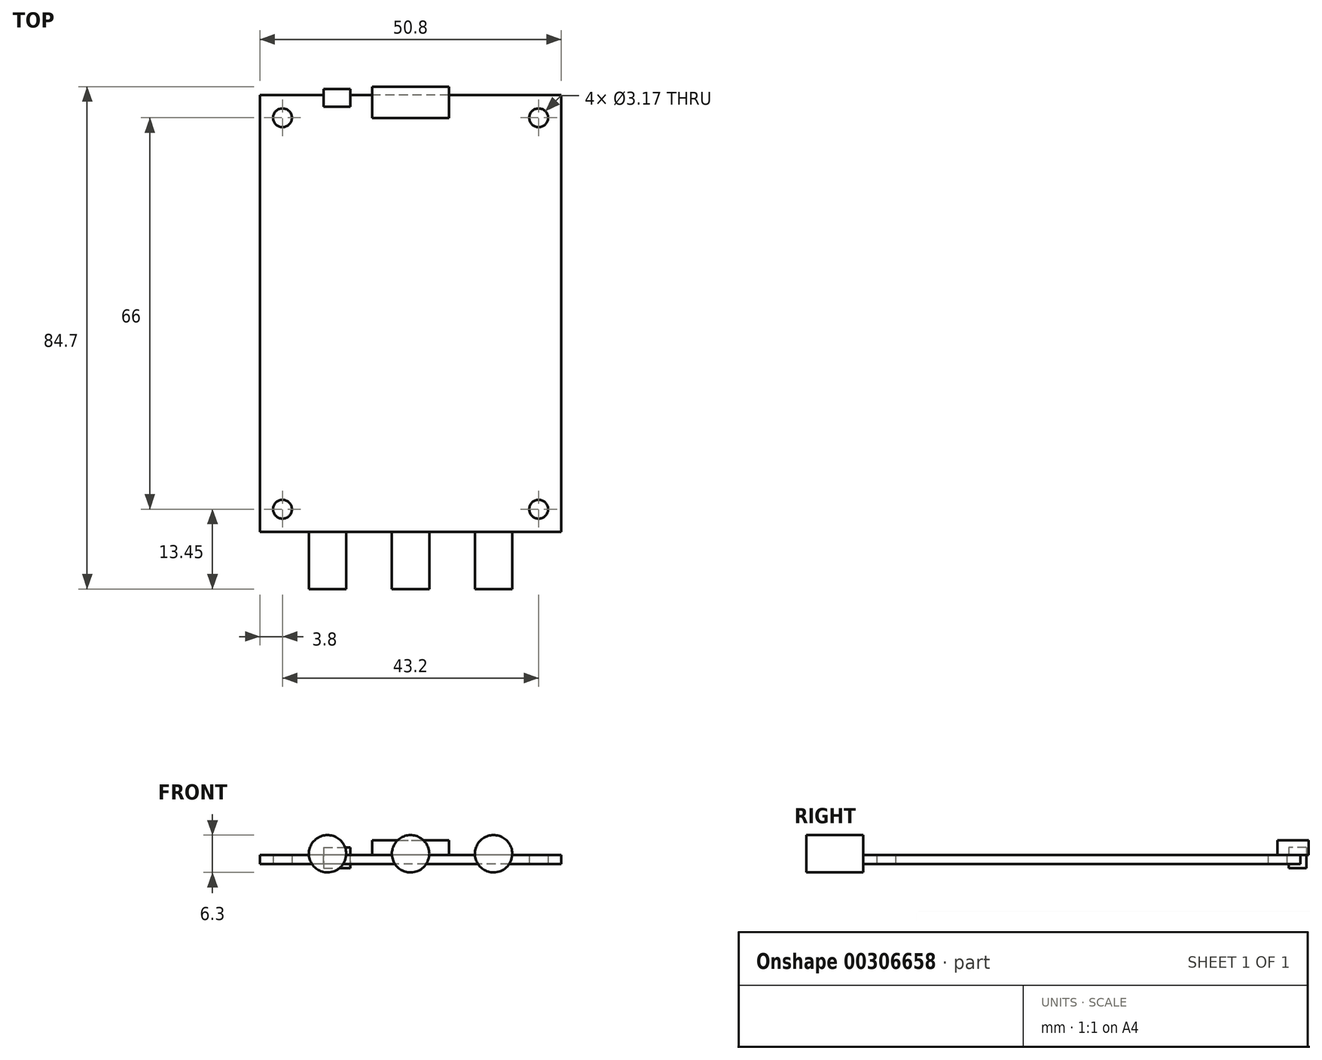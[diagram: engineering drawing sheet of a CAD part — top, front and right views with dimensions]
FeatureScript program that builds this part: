
annotation { "Feature Type Name" : "Feature", "Feature Type Description" : "" }
export const myFeature = defineFeature(function(context is Context, id is Id, definition is map)
    precondition{}
    {
        {
            var Q0;
            Q0=qCreatedBy(makeId("Top.planeOp"),FACE);
            var sketch = newSketch(context, id + "F0", { "sketchPlane" : qUnion([Q0])});
            skLineSegment(sketch, "E0.bottom", {"start": v(25.4, -36.85) * mm, "end": v(-25.4, -36.85) * mm});
            skLineSegment(sketch, "E0.top", {"start": v(25.4, 36.85) * mm, "end": v(-25.4, 36.85) * mm});
            skLineSegment(sketch, "E0.left", {"start": v(25.4, -36.85) * mm, "end": v(25.4, 36.85) * mm});
            skLineSegment(sketch, "E0.right", {"start": v(-25.4, -36.85) * mm, "end": v(-25.4, 36.85) * mm});
            skPoint(sketch, "E0.middle", {"position": v(0, 0) * mm});
            skLineSegment(sketch, "E1.bottom", {"start": v(21.6, -33) * mm, "end": v(-21.6, -33) * mm, "construction": true});
            skLineSegment(sketch, "E1.top", {"start": v(21.6, 33) * mm, "end": v(-21.6, 33) * mm, "construction": true});
            skLineSegment(sketch, "E1.left", {"start": v(21.6, -33) * mm, "end": v(21.6, 33) * mm, "construction": true});
            skLineSegment(sketch, "E1.right", {"start": v(-21.6, -33) * mm, "end": v(-21.6, 33) * mm, "construction": true});
            skCircle(sketch, "E2", {"center": v(-21.6, 33) * mm, "radius": 1.59 * mm});
            skCircle(sketch, "E3", {"center": v(21.6, 33) * mm, "radius": 1.59 * mm});
            skCircle(sketch, "E4", {"center": v(21.6, -33) * mm, "radius": 1.59 * mm});
            skCircle(sketch, "E5", {"center": v(-21.6, -33) * mm, "radius": 1.59 * mm});
            skPoint(sketch, "E6", {"position": v(0, -36.85) * mm});
            skLineSegment(sketch, "E7.bottom", {"start": v(3.15, -36.85) * mm, "end": v(-3.15, -36.85) * mm, "construction": true});
            skLineSegment(sketch, "E7.top", {"start": v(3.15, -46.45) * mm, "end": v(-3.15, -46.45) * mm, "construction": true});
            skLineSegment(sketch, "E7.left", {"start": v(3.15, -36.85) * mm, "end": v(3.15, -46.45) * mm, "construction": true});
            skLineSegment(sketch, "E7.right", {"start": v(-3.15, -36.85) * mm, "end": v(-3.15, -46.45) * mm, "construction": true});
            skPoint(sketch, "E7.middle", {"position": v(0, -41.65) * mm});
            skLineSegment(sketch, "E8.bottom", {"start": v(17.15, -36.85) * mm, "end": v(10.85, -36.85) * mm, "construction": true});
            skLineSegment(sketch, "E8.top", {"start": v(17.15, -46.45) * mm, "end": v(10.85, -46.45) * mm, "construction": true});
            skLineSegment(sketch, "E8.left", {"start": v(17.15, -36.85) * mm, "end": v(17.15, -46.45) * mm, "construction": true});
            skLineSegment(sketch, "E8.right", {"start": v(10.85, -36.85) * mm, "end": v(10.85, -46.45) * mm, "construction": true});
            skPoint(sketch, "E8.middle", {"position": v(14, -41.65) * mm});
            skLineSegment(sketch, "E9.bottom", {"start": v(-10.85, -36.85) * mm, "end": v(-17.15, -36.85) * mm, "construction": true});
            skLineSegment(sketch, "E9.top", {"start": v(-10.85, -46.45) * mm, "end": v(-17.15, -46.45) * mm, "construction": true});
            skLineSegment(sketch, "E9.left", {"start": v(-10.85, -36.85) * mm, "end": v(-10.85, -46.45) * mm, "construction": true});
            skLineSegment(sketch, "E9.right", {"start": v(-17.15, -36.85) * mm, "end": v(-17.15, -46.45) * mm, "construction": true});
            skPoint(sketch, "E9.middle", {"position": v(-14, -41.65) * mm});
            skLineSegment(sketch, "E10.bottom", {"start": v(6.45, 38.25) * mm, "end": v(-6.45, 38.25) * mm, "construction": true});
            skLineSegment(sketch, "E10.top", {"start": v(6.45, 32.95) * mm, "end": v(-6.45, 32.95) * mm, "construction": true});
            skLineSegment(sketch, "E10.left", {"start": v(6.45, 38.25) * mm, "end": v(6.45, 32.95) * mm, "construction": true});
            skLineSegment(sketch, "E10.right", {"start": v(-6.45, 38.25) * mm, "end": v(-6.45, 32.95) * mm, "construction": true});
            skPoint(sketch, "E10.middle", {"position": v(0, 35.6) * mm});
            skPoint(sketch, "E10.middle.positionSnap0", {"position": v(0, 36.85) * mm});
            skPoint(sketch, "E10.centerSnap0", {"position": v(0, 36.85) * mm});
            skLineSegment(sketch, "E11.bottom", {"start": v(-14.65, 37.85) * mm, "end": v(-10.15, 37.85) * mm});
            skLineSegment(sketch, "E11.top", {"start": v(-14.65, 34.85) * mm, "end": v(-10.15, 34.85) * mm});
            skLineSegment(sketch, "E11.left", {"start": v(-14.65, 37.85) * mm, "end": v(-14.65, 34.85) * mm});
            skLineSegment(sketch, "E11.right", {"start": v(-10.15, 37.85) * mm, "end": v(-10.15, 34.85) * mm});
            skPoint(sketch, "E12", {"position": v(-12.4, 37.85) * mm});
            skSolve(sketch);
        }
        {
            var Q0;
            Q0=qCreatedBy(makeId("Front.planeOp"),FACE);
            var sketch = newSketch(context, id + "F1", { "sketchPlane" : qUnion([Q0])});
            skCircle(sketch, "E13", {"center": v(0, 1.7) * mm, "radius": 3.15 * mm});
            skCircle(sketch, "E14", {"center": v(14, 1.7) * mm, "radius": 3.15 * mm});
            skCircle(sketch, "E15", {"center": v(-14, 1.7) * mm, "radius": 3.15 * mm});
            skSolve(sketch);
        }
        {
            var Q0;
            Q0=qCreatedBy(makeId("Front.planeOp"),FACE);
            var sketch = newSketch(context, id + "F2", { "sketchPlane" : qUnion([Q0])});
            skLineSegment(sketch, "E16.bottom", {"start": v(6.45, 1.5) * mm, "end": v(-6.45, 1.5) * mm});
            skLineSegment(sketch, "E16.top", {"start": v(-6.45, 4) * mm, "end": v(6.45, 4) * mm});
            skLineSegment(sketch, "E16.left", {"start": v(-6.45, 1.5) * mm, "end": v(-6.45, 4) * mm});
            skLineSegment(sketch, "E16.right", {"start": v(6.45, 1.5) * mm, "end": v(6.45, 4) * mm});
            skPoint(sketch, "E16.middle", {"position": v(0, 2.75) * mm});
            skSolve(sketch);
        }
        {
            var Q0;
            Q0=makeQuery(id+"F0.imprint","IMPRINT",FACE,{"disambiguationData":[TD([[makeQuery(id+"F0.imprint","IMPRINT",EDGE,{"derivedFrom":sQuery(id+"F0.wireOp",EDGE,"E0.top")}),1.0]])]});
            var Q1;
            {var subQ5=sQuery(id+"F0.wireOp",EDGE,"E11.top");Q1=makeQuery(id+"F0.imprint","IMPRINT",FACE,{"disambiguationData":[TD([[makeQuery(id+"F0.imprint","IMPRINT",EDGE,{"derivedFrom":subQ5}),1.0]])]});}
            extrude(context, id + "F3", {"entities" : qUnion([Q0, Q1]), "depth" : 1.5 * mm});
        }
        {
            var Q0;
            Q0=makeQuery(id+"F1.imprint","IMPRINT",FACE,{"disambiguationData":[TD([[makeQuery(id+"F1.imprint","IMPRINT",EDGE,{"derivedFrom":sQuery(id+"F1.wireOp",EDGE,"E15")}),1.0]])]});
            var Q1;
            Q1=makeQuery(id+"F1.imprint","IMPRINT",FACE,{"disambiguationData":[TD([[makeQuery(id+"F1.imprint","IMPRINT",EDGE,{"derivedFrom":sQuery(id+"F1.wireOp",EDGE,"E13")}),1.0]])]});
            var Q2;
            Q2=makeQuery(id+"F1.imprint","IMPRINT",FACE,{"disambiguationData":[TD([[makeQuery(id+"F1.imprint","IMPRINT",EDGE,{"derivedFrom":sQuery(id+"F1.wireOp",EDGE,"E14")}),1.0]])]});
            var Q3;
            Q3=sQuery(id+"F0.wireOp",VERTEX,"E7.right.end");
            var Q4;
            Q4=sQuery(id+"F0.wireOp",VERTEX,"E7.right.start");
            extrude(context, id + "F4", {"entities" : qUnion([Q0, Q1, Q2]), "operationType" : NewBodyOperationType.ADD, "endBound" : BoundingType.UP_TO_VERTEX, "endBoundEntityVertex" : qUnion([Q3]), "depth" : 25 * mm, "hasSecondDirection" : true, "secondDirectionBound" : SecondDirectionBoundingType.UP_TO_VERTEX, "secondDirectionOppositeDirection" : false, "secondDirectionBoundEntityVertex" : qUnion([Q4]), "secondDirectionDepth" : 25 * mm});
        }
        {
            var Q0;
            Q0 = qSketchRegion(id + "F2", true);
            var Q1;
            Q1=sQuery(id+"F0.wireOp",VERTEX,"E10.bottom.start");
            var Q2;
            Q2=sQuery(id+"F0.wireOp",VERTEX,"E10.left.end");
            extrude(context, id + "F5", {"entities" : qUnion([Q0]), "operationType" : NewBodyOperationType.ADD, "endBound" : BoundingType.UP_TO_VERTEX, "oppositeDirection" : true, "endBoundEntityVertex" : qUnion([Q1]), "depth" : 25 * mm, "hasSecondDirection" : true, "secondDirectionBound" : SecondDirectionBoundingType.UP_TO_VERTEX, "secondDirectionOppositeDirection" : true, "secondDirectionBoundEntityVertex" : qUnion([Q2]), "secondDirectionDepth" : 25 * mm});
        }
        {
            var Q0;
            {var subQ5=sQuery(id+"F0.wireOp",EDGE,"E11.top");Q0=makeQuery(id+"F0.imprint","IMPRINT",FACE,{"disambiguationData":[TD([[makeQuery(id+"F0.imprint","IMPRINT",EDGE,{"derivedFrom":subQ5}),1.0]])]});}
            var Q1;
            {var subQ5=sQuery(id+"F0.wireOp",EDGE,"E11.bottom");Q1=makeQuery(id+"F0.imprint","IMPRINT",FACE,{"disambiguationData":[TD([[makeQuery(id+"F0.imprint","IMPRINT",EDGE,{"derivedFrom":subQ5}),-1.0]])]});}
            extrude(context, id + "F6", {"entities" : qUnion([Q0, Q1]), "operationType" : NewBodyOperationType.ADD, "depth" : 2.75 * mm, "hasSecondDirection" : true, "secondDirectionOppositeDirection" : true, "secondDirectionDepth" : .75 * mm});
        }
    });
